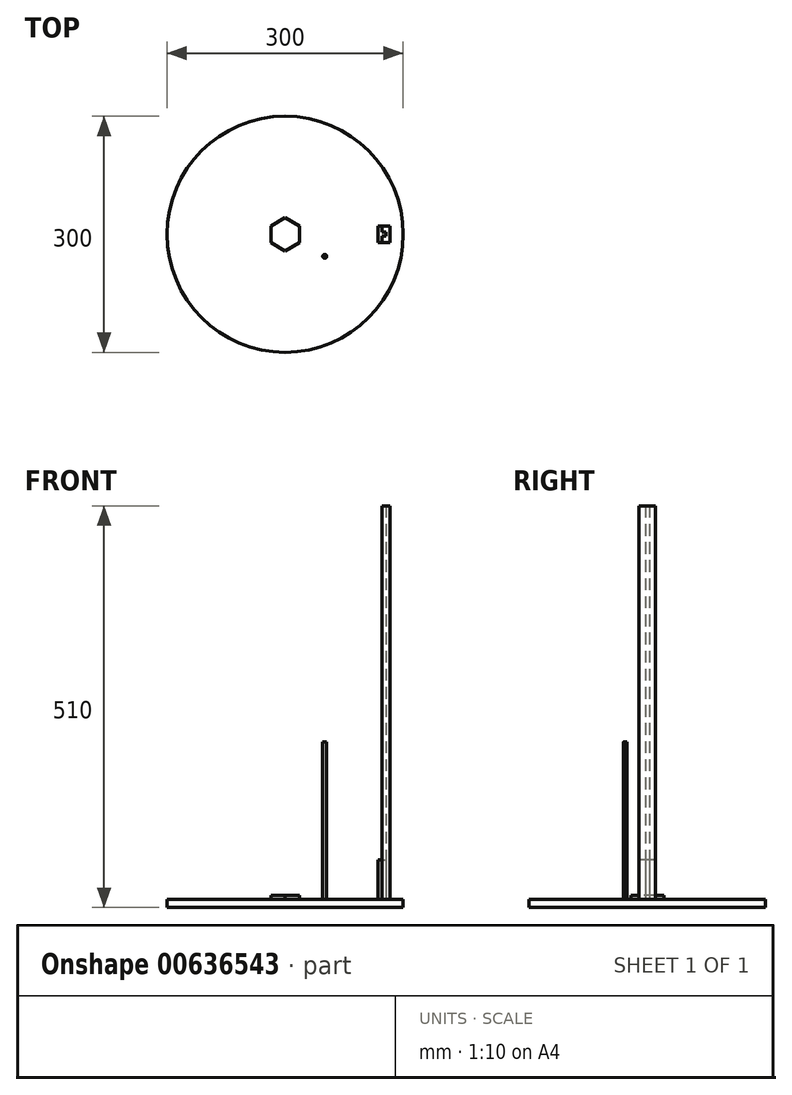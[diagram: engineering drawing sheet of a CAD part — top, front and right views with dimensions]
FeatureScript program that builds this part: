
annotation { "Feature Type Name" : "Feature", "Feature Type Description" : "" }
export const myFeature = defineFeature(function(context is Context, id is Id, definition is map)
    precondition{}
    {
        {
            var Q0;
            Q0=qCreatedBy(makeId("Top.planeOp"),FACE);
            var sketch = newSketch(context, id + "F0", { "sketchPlane" : qUnion([Q0])});
            skCircle(sketch, "E0.cCircle", {"center": v(0, 0) * mm, "radius": 18.2 * mm, "construction": true});
            skLineSegment(sketch, "E0.0", {"start": v(18.2, 10.5) * mm, "end": v(18.2, -10.5) * mm});
            skLineSegment(sketch, "E0.1", {"start": v(18.2, -10.5) * mm, "end": v(0, -21) * mm});
            skLineSegment(sketch, "E0.2", {"start": v(0, -21) * mm, "end": v(-18.2, -10.5) * mm});
            skLineSegment(sketch, "E0.3", {"start": v(-18.2, -10.5) * mm, "end": v(-18.2, 10.5) * mm});
            skLineSegment(sketch, "E0.4", {"start": v(-18.2, 10.5) * mm, "end": v(0, 21) * mm});
            skLineSegment(sketch, "E0.5", {"start": v(0, 21) * mm, "end": v(18.2, 10.5) * mm});
            skPoint(sketch, "E0.0.midPoint", {"position": v(18.2, 0) * mm});
            skCircle(sketch, "E1", {"center": v(0, 0) * mm, "radius": 150 * mm});
            skLineSegment(sketch, "E2.0", {"start": v(118.2, 10.5) * mm, "end": v(118.2, -10.5) * mm});
            skLineSegment(sketch, "E3.0", {"start": v(123.2, 10.5) * mm, "end": v(123.2, 2.53) * mm});
            skLineSegment(sketch, "E4", {"start": v(118.2, 10.5) * mm, "end": v(123.2, 10.5) * mm});
            skLineSegment(sketch, "E5", {"start": v(118.2, -10.5) * mm, "end": v(123.2, -10.5) * mm});
            skLineSegment(sketch, "E6", {"start": v(123.2, 10.5) * mm, "end": v(133.2, 10.5) * mm});
            skLineSegment(sketch, "E7", {"start": v(133.2, 10.5) * mm, "end": v(133.2, -10.5) * mm});
            skLineSegment(sketch, "E8", {"start": v(133.2, -10.5) * mm, "end": v(123.2, -10.5) * mm});
            skLineSegment(sketch, "E9", {"start": v(123.2, 0) * mm, "end": v(130.02, 0) * mm, "construction": true});
            skPoint(sketch, "E9.endSnap0", {"position": v(123.2, 0) * mm});
            skLineSegment(sketch, "E10.bottom", {"start": v(123.2, 2.53) * mm, "end": v(128.2, 2.53) * mm});
            skLineSegment(sketch, "E10.top", {"start": v(123.2, -2.53) * mm, "end": v(128.2, -2.53) * mm});
            skLineSegment(sketch, "E10.right", {"start": v(128.2, 2.53) * mm, "end": v(128.2, -2.53) * mm});
            skPoint(sketch, "E10.middle", {"position": v(125.7, 0) * mm});
            skLineSegment(sketch, "E11.trimOffspring", {"start": v(123.2, -2.53) * mm, "end": v(123.2, -10.5) * mm});
            skCircle(sketch, "E12", {"center": v(50.27, -28.05) * mm, "radius": 2.5 * mm});
            skSolve(sketch);
        }
        {
            var Q0;
            Q0=makeQuery(id+"F0.imprint","IMPRINT",FACE,{"disambiguationData":[TD([[makeQuery(id+"F0.imprint","IMPRINT",EDGE,{"derivedFrom":sQuery(id+"F0.wireOp",EDGE,"E3.0")}),1.0]])]});
            extrude(context, id + "F1", {"entities" : qUnion([Q0]), "depth" : 500 * mm, "offsetDistance" : 25 * mm});
        }
        {
            var Q0;
            Q0=makeQuery(id+"F0.imprint","IMPRINT",FACE,{"disambiguationData":[TD([[makeQuery(id+"F0.imprint","IMPRINT",EDGE,{"derivedFrom":sQuery(id+"F0.wireOp",EDGE,"E0.0")}),-1.0]])]});
            extrude(context, id + "F2", {"entities" : qUnion([Q0]), "depth" : 5 * mm, "offsetDistance" : 25 * mm});
        }
        {
            var Q0;
            Q0=makeQuery(id+"F0.imprint","IMPRINT",FACE,{"disambiguationData":[TD([[makeQuery(id+"F0.imprint","IMPRINT",EDGE,{"derivedFrom":sQuery(id+"F0.wireOp",EDGE,"E2.0")}),1.0]])]});
            extrude(context, id + "F3", {"entities" : qUnion([Q0]), "depth" : 50 * mm, "offsetDistance" : 25 * mm});
        }
        {
            var Q0;
            Q0=makeQuery(id+"F0.imprint","IMPRINT",FACE,{"disambiguationData":[TD([[makeQuery(id+"F0.imprint","IMPRINT",EDGE,{"derivedFrom":sQuery(id+"F0.wireOp",EDGE,"E12")}),1.0]])]});
            extrude(context, id + "F4", {"entities" : qUnion([Q0]), "depth" : 200 * mm, "offsetDistance" : 25 * mm});
        }
        {
            var Q0;
            Q0=makeQuery(id+"F0.imprint","IMPRINT",FACE,{"disambiguationData":[TD([[makeQuery(id+"F0.imprint","IMPRINT",EDGE,{"derivedFrom":sQuery(id+"F0.wireOp",EDGE,"E0.0")}),1.0]])]});
            var Q1;
            Q1=makeQuery(id+"F0.imprint","IMPRINT",FACE,{"disambiguationData":[TD([[makeQuery(id+"F0.imprint","IMPRINT",EDGE,{"derivedFrom":sQuery(id+"F0.wireOp",EDGE,"E3.0")}),1.0]])]});
            var Q2;
            Q2=makeQuery(id+"F0.imprint","IMPRINT",FACE,{"disambiguationData":[TD([[makeQuery(id+"F0.imprint","IMPRINT",EDGE,{"derivedFrom":sQuery(id+"F0.wireOp",EDGE,"E2.0")}),1.0]])]});
            var Q3;
            Q3=makeQuery(id+"F0.imprint","IMPRINT",FACE,{"disambiguationData":[TD([[makeQuery(id+"F0.imprint","IMPRINT",EDGE,{"derivedFrom":sQuery(id+"F0.wireOp",EDGE,"E0.0")}),-1.0]])]});
            var Q4;
            Q4=makeQuery(id+"F0.imprint","IMPRINT",FACE,{"disambiguationData":[TD([[makeQuery(id+"F0.imprint","IMPRINT",EDGE,{"derivedFrom":sQuery(id+"F0.wireOp",EDGE,"E12")}),1.0]])]});
            extrude(context, id + "F5", {"entities" : qUnion([Q0, Q1, Q2, Q3, Q4]), "oppositeDirection" : true, "depth" : 10 * mm, "offsetDistance" : 25 * mm});
        }
    });
